# Revit family: Primo_EC
name_source: partatom
category: Mechanical Equipment
units: mm (PartAtom-declared; Revit-internal decimal feet)

## family parameters
Always vertical = Yes
Classification = None
Cut with Voids When Loaded = No
Part Type = Normal
Room Calculation Point = No
Round Connector Dimension = Use Diameter
Shared = No
Work Plane-Based = No

## types (12) — shared parameters
00_20_Manufacturer = Blauberg
00_20_Name = Inline mixed flow fan
Casing Material = Plastic, opaque, black
Corner_mount = No
Description = For round channels
Frequency = 50 Hz
Handle = 29 mm
Handle 1 = 31 mm  [stored 0.101706 ft]
Load Classification = HVAC
Maintenance zone material = <By Category>
Manufacturer = Blauberg
Number of Fase = 1
Temperature of moving air = -25...+55 °C
URL = https://blaubergventilatoren.de
Voltage = 230 V
Z = 150 mm  [stored 0.492126 ft]
zero-valued in all types: Default Elevation

## per-type parameters (varying)
- Primo 150: A1=104 mm; A2=207 mm; Amperage=0 A; Apparent Load=46 VA; B1=320 mm; C1=129 mm; Casing=Casing : 150; D=149 mm  [stored 0.488845 ft]; Diameter=149 mm  [stored 0.488845 ft]; Dy=144 mm  [stored 0.472441 ft]; Frame_M=Yes; H=267 mm; Height=267 mm; K=38 mm  [stored 0.124672 ft]; L=301 mm; Length=301 mm; Maximum Air Flow=600.0 m³/h; Power=45 W; R=75 mm  [stored 0.246063 ft]; Ry=72 mm  [stored 0.23622 ft]; Sound pressure level at 3 m distance=37 dBA; W=247 mm; Width=247 mm; X=94 mm; a=134 mm; b=151 mm  [stored 0.495407 ft]; frame=No; Сonnector at an angle=No; Сonnector vert=Yes
- Primo 250: A1=141 mm; A2=282 mm; Amperage=1 A; Apparent Load=193 VA; B1=450 mm; C1=169 mm; Casing=Casing : 250; D=249 mm; Diameter=249 mm; Dy=244 mm; Frame_M=Yes; H=342 mm; Height=342 mm; K=36 mm; L=293 mm; Length=293 mm; Maximum Air Flow=1715.0 m³/h; Power=188 W; R=125 mm  [stored 0.410105 ft]; Ry=122 mm  [stored 0.400262 ft]; Sound pressure level at 3 m distance=43 dBA; W=327 mm; Width=327 mm; X=131 mm; a=171 mm  [stored 0.561024 ft]; b=147 mm; frame=No; Сonnector at an angle=No; Сonnector vert=Yes
- Primo 200: A1=124 mm; A2=248 mm; Amperage=1 A; Apparent Load=117 VA; B1=400 mm; C1=152 mm; Casing=Casing : 200; D=199 mm; Diameter=199 mm; Dy=194 mm; Frame_M=Yes; H=308 mm; Height=308 mm; K=38 mm  [stored 0.124672 ft]; L=302 mm; Length=302 mm; Maximum Air Flow=1140.0 m³/h; Power=113 W; R=99 mm; Ry=97 mm; Sound pressure level at 3 m distance=42 dBA; W=293 mm; Width=293 mm; X=114 mm; a=154 mm  [stored 0.505249 ft]; b=151 mm  [stored 0.495407 ft]; frame=No; Сonnector at an angle=No; Сonnector vert=Yes
- Primo 355: A1=190 mm; A2=379 mm; Amperage=1 A; Apparent Load=152 VA; B1=566 mm; C1=203 mm; Casing=Casing : 200; D=355 mm; Diameter=355 mm; Dy=350 mm; Frame_M=No; H=439 mm; Height=439 mm; K=56 mm; L=372 mm; Length=372 mm; Maximum Air Flow=2485.0 m³/h; Power=150 W; R=178 mm  [stored 0.58399 ft]; Ry=175 mm  [stored 0.574147 ft]; Sound pressure level at 3 m distance=43 dBA; W=406 mm; Width=566 mm; X=180 mm; a=220 mm; b=186 mm  [stored 0.610236 ft]; frame=Yes; Сonnector at an angle=Yes; Сonnector vert=No
- Primo 400: A1=212 mm; A2=424 mm; Amperage=1 A; Apparent Load=225 VA; B1=623 mm; C1=226 mm; Casing=Casing : 200; D=400 mm; Diameter=400 mm; Dy=395 mm; Frame_M=No; H=484 mm; Height=484 mm; K=66 mm; L=415 mm; Length=415 mm; Maximum Air Flow=3350.0 m³/h; Power=224 W; R=200 mm; Ry=198 mm; Sound pressure level at 3 m distance=43 dBA; W=451 mm; Width=623 mm; X=202 mm; a=242 mm; b=208 mm; frame=Yes; Сonnector at an angle=Yes; Сonnector vert=No
- Primo EC 150: A1=104 mm; A2=207 mm; Amperage=0 A; Apparent Load=110 VA; B1=320 mm; C1=129 mm; Casing=Casing : 150; D=149 mm  [stored 0.488845 ft]; Diameter=149 mm  [stored 0.488845 ft]; Dy=144 mm  [stored 0.472441 ft]; Frame_M=Yes; H=267 mm; Height=267 mm; K=38 mm  [stored 0.124672 ft]; L=301 mm; Length=301 mm; Maximum Air Flow=700.0 m³/h; Power=54 W; R=75 mm  [stored 0.246063 ft]; Ry=72 mm  [stored 0.23622 ft]; Sound pressure level at 3 m distance=49 dBA; W=247 mm; Width=247 mm; X=94 mm; a=134 mm; b=151 mm  [stored 0.495407 ft]; frame=No; Сonnector at an angle=No; Сonnector vert=Yes
- Primo EC 200: A1=124 mm; A2=248 mm; Amperage=1 A; Apparent Load=221 VA; B1=400 mm; C1=152 mm; Casing=Casing : 200; D=199 mm; Diameter=199 mm; Dy=194 mm; Frame_M=Yes; H=308 mm; Height=308 mm; K=38 mm  [stored 0.124672 ft]; L=302 mm; Length=302 mm; Maximum Air Flow=1250.0 m³/h; Power=121 W; R=99 mm; Ry=97 mm; Sound pressure level at 3 m distance=50 dBA; W=293 mm; Width=293 mm; X=114 mm; a=154 mm  [stored 0.505249 ft]; b=151 mm  [stored 0.495407 ft]; frame=No; Сonnector at an angle=No; Сonnector vert=Yes
- Primo EC 250: A1=141 mm; A2=282 mm; Amperage=1 A; Apparent Load=308 VA; B1=450 mm; C1=169 mm; Casing=Casing : 250; D=249 mm; Diameter=249 mm; Dy=244 mm; Frame_M=Yes; H=342 mm; Height=342 mm; K=36 mm; L=293 mm; Length=293 mm; Maximum Air Flow=1800.0 m³/h; Power=168 W; R=125 mm  [stored 0.410105 ft]; Ry=122 mm  [stored 0.400262 ft]; Sound pressure level at 3 m distance=49 dBA; W=327 mm; Width=327 mm; X=131 mm; a=171 mm  [stored 0.561024 ft]; b=147 mm; frame=No; Сonnector at an angle=No; Сonnector vert=Yes
- Primo EC 315 max: A1=190 mm; A2=379 mm; Amperage=2 A; Apparent Load=359 VA; B1=566 mm; C1=203 mm; Casing=Casing : 200; D=315 mm; Diameter=315 mm; Dy=310 mm; Frame_M=No; H=439 mm; Height=439 mm; K=56 mm; L=372 mm; Length=372 mm; Maximum Air Flow=3250.0 m³/h; Power=353 W; R=158 mm; Ry=155 mm  [stored 0.50853 ft]; Sound pressure level at 3 m distance=55 dBA; W=406 mm; Width=566 mm; X=180 mm; a=220 mm; b=186 mm  [stored 0.610236 ft]; frame=Yes; Сonnector at an angle=Yes; Сonnector vert=No
- Primo EC 400: A1=212 mm; A2=424 mm; Amperage=3 A; Apparent Load=743 VA; B1=623 mm; C1=226 mm; Casing=Casing : 200; D=400 mm; Diameter=400 mm; Dy=395 mm; Frame_M=No; H=484 mm; Height=484 mm; K=66 mm; L=415 mm; Length=415 mm; Maximum Air Flow=5700.0 m³/h; Power=726 W; R=200 mm; Ry=198 mm; Sound pressure level at 3 m distance=60 dBA; W=451 mm; Width=623 mm; X=202 mm; a=242 mm; b=208 mm; frame=Yes; Сonnector at an angle=Yes; Сonnector vert=No
- Primo EC 355: A1=190 mm; A2=379 mm; Amperage=2 A; Apparent Load=359 VA; B1=566 mm; C1=203 mm; Casing=Casing : 200; D=355 mm; Diameter=355 mm; Dy=350 mm; Frame_M=No; H=439 mm; Height=439 mm; K=56 mm; L=372 mm; Length=372 mm; Maximum Air Flow=3685.0 m³/h; Power=353 W; R=178 mm  [stored 0.58399 ft]; Ry=175 mm  [stored 0.574147 ft]; Sound pressure level at 3 m distance=55 dBA; W=406 mm; Width=566 mm; X=180 mm; a=220 mm; b=186 mm  [stored 0.610236 ft]; frame=Yes; Сonnector at an angle=Yes; Сonnector vert=No
- Primo EC 355 max: A1=190 mm; A2=379 mm; Amperage=3 A; Apparent Load=713 VA; B1=566 mm; C1=203 mm; Casing=Casing : 200; D=355 mm; Diameter=355 mm; Dy=350 mm; Frame_M=No; H=439 mm; Height=439 mm; K=56 mm; L=372 mm; Length=372 mm; Maximum Air Flow=4630.0 m³/h; Power=701 W; R=178 mm  [stored 0.58399 ft]; Ry=175 mm  [stored 0.574147 ft]; Sound pressure level at 3 m distance=60 dBA; W=406 mm; Width=566 mm; X=180 mm; a=220 mm; b=186 mm  [stored 0.610236 ft]; frame=Yes; Сonnector at an angle=Yes; Сonnector vert=No

note: column(s) folded — value = type name in every type: 00_20_Type

note: [stored X ft] marks values corroborated as IEEE doubles in the binary element streams (Revit-internal decimal feet)
